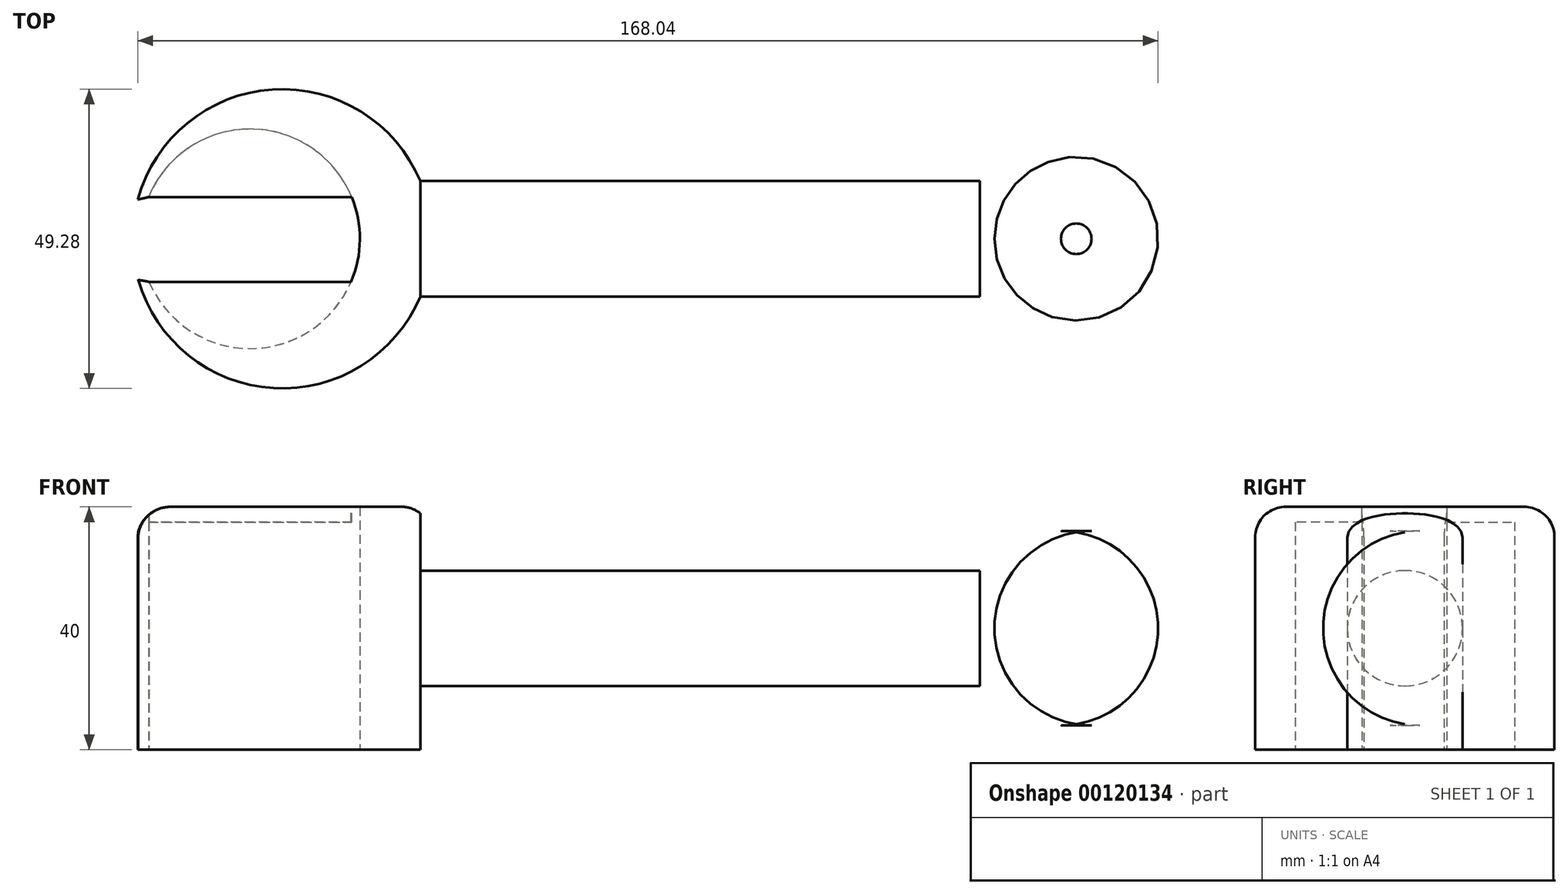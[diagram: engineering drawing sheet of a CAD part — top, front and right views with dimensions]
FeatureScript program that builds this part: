
annotation { "Feature Type Name" : "Feature", "Feature Type Description" : "" }
export const myFeature = defineFeature(function(context is Context, id is Id, definition is map)
    precondition{}
    {
        {
            var Q0;
            Q0=qCreatedBy(makeId("Top.planeOp"),FACE);
            var sketch = newSketch(context, id + "F0", { "sketchPlane" : qUnion([Q0])});
            skArc(sketch, "E0", {"start": v(-60.08, 17.67) * mm, "mid": v(-84.42, 32.76) * mm, "end": v(-106.6, 14.63) * mm});
            skLineSegment(sketch, "E1.bottom", {"start": v(-60.08, 17.67) * mm, "end": v(32.07, 17.67) * mm});
            skLineSegment(sketch, "E1.top", {"start": v(-60.08, -1.33) * mm, "end": v(32.07, -1.33) * mm});
            skPoint(sketch, "E2.start.orphan", {"position": v(39.84, 8.17) * mm});
            skPoint(sketch, "E3.end.orphan", {"position": v(-60.08, -1.33) * mm});
            skPoint(sketch, "E4.visualSharp", {"position": v(-82.82, 17.67) * mm});
            skPoint(sketch, "E5.visualSharp", {"position": v(-69.5, 8.17) * mm});
            skPoint(sketch, "E6.visualSharp", {"position": v(-82.82, -1.33) * mm});
            skLineSegment(sketch, "E7", {"start": v(-82.82, -5.13) * mm, "end": v(-82.82, -5.13) * mm});
            skArc(sketch, "E8.trimOffspring", {"start": v(-106.51, 1.41) * mm, "mid": v(-84.27, -16.43) * mm, "end": v(-60.08, -1.33) * mm});
            skPoint(sketch, "E9.orphan", {"position": v(-82.82, 22.17) * mm});
            skPoint(sketch, "E10.orphan", {"position": v(-69.5, 4.34) * mm});
            skPoint(sketch, "E11.visualSharp", {"position": v(-90.88, 19.61) * mm});
            skPoint(sketch, "E12.orphan", {"position": v(45.12, 19.04) * mm});
            skPoint(sketch, "E13.visualSharp", {"position": v(-91.65, -2.7) * mm});
            skLineSegment(sketch, "E14", {"start": v(-106.6, 14.63) * mm, "end": v(-104.83, 15.04) * mm});
            skLineSegment(sketch, "E15", {"start": v(-106.51, 1.41) * mm, "end": v(-104.74, 1.1) * mm});
            skLineSegment(sketch, "E16", {"start": v(-60.08, 17.67) * mm, "end": v(-60.08, -1.33) * mm});
            skPoint(sketch, "E17.orphan", {"position": v(39.84, 17.67) * mm});
            skPoint(sketch, "E18.center.orphan", {"position": v(45.12, 8.17) * mm});
            skPoint(sketch, "E19.orphan", {"position": v(39.84, -1.33) * mm});
            skPoint(sketch, "E20.center.orphan", {"position": v(47.96, 8.17) * mm});
            skArc(sketch, "E21", {"start": v(-104.74, 1.1) * mm, "mid": v(-70.03, 8.28) * mm, "end": v(-104.83, 15.04) * mm});
            skPoint(sketch, "E22.orphan", {"position": v(-90.88, 18.29) * mm});
            skPoint(sketch, "E23.orphan", {"position": v(-91.65, -1.28) * mm});
            skPoint(sketch, "E24.center.orphan", {"position": v(-89.28, 8.17) * mm});
            skPoint(sketch, "E25.right.end.orphan", {"position": v(57.82, -3.93) * mm});
            skArc(sketch, "E26", {"start": v(32.07, -1.33) * mm, "mid": v(66.48, 8.17) * mm, "end": v(32.07, 17.67) * mm});
            skPoint(sketch, "E27.end.orphan", {"position": v(36.17, -3.93) * mm});
            skPoint(sketch, "E28.left.end.orphan", {"position": v(36.17, 20.27) * mm});
            skPoint(sketch, "E28.bottom.start.orphan", {"position": v(36.17, 21.83) * mm});
            skCircle(sketch, "E29", {"center": v(-88.1, 8.17) * mm, "radius": 16.54 * mm});
            skPoint(sketch, "E30.center.orphan", {"position": v(46.23, 8.17) * mm});
            skPoint(sketch, "E31.trimOffspring.end.orphan", {"position": v(36.17, -1.33) * mm});
            skPoint(sketch, "E32.orphan", {"position": v(36.17, 17.67) * mm});
            skLineSegment(sketch, "E33", {"start": v(32.07, -1.33) * mm, "end": v(32.07, 17.67) * mm});
            skSolve(sketch);
        }
        {
            var Q0;
            Q0=makeQuery(id+"F0.imprint","IMPRINT",FACE,{"disambiguationData":[TD([[makeQuery(id+"F0.imprint","IMPRINT",EDGE,{"derivedFrom":sQuery(id+"F0.wireOp",EDGE,"E0")}),1.0]])]});
            extrude(context, id + "F1", {"entities" : qUnion([Q0]), "depth" : 20 * mm, "hasSecondDirection" : true, "secondDirectionOppositeDirection" : true, "secondDirectionDepth" : 20 * mm});
        }
        {
            var Q0;
            Q0=makeQuery(id+"F0.imprint","IMPRINT",FACE,{"disambiguationData":[TD([[makeQuery(id+"F0.imprint","IMPRINT",EDGE,{"derivedFrom":sQuery(id+"F0.wireOp",EDGE,"E1.bottom")}),-1.0]])]});
            extrude(context, id + "F2", {"entities" : qUnion([Q0]), "operationType" : NewBodyOperationType.ADD, "depth" : 9.5 * mm, "hasSecondDirection" : true, "secondDirectionOppositeDirection" : true, "secondDirectionDepth" : 9.5 * mm});
        }
        {
            var Q0;
            Q0=makeQuery(id+"F0.imprint","IMPRINT",FACE,{"disambiguationData":[TD([[makeQuery(id+"F0.imprint","IMPRINT",EDGE,{"derivedFrom":sQuery(id+"F0.wireOp",EDGE,"E26")}),1.0]])]});
            extrude(context, id + "F3", {"entities" : qUnion([Q0]), "depth" : 16 * mm, "hasSecondDirection" : true, "secondDirectionOppositeDirection" : true, "secondDirectionDepth" : 16 * mm});
        }
        {
            var Q0;
            Q0=makeQuery(id+"F3.opExtrude","CAP_EDGE",EDGE,{"disambiguationData":[OSD([sQuery(id+"F0.wireOp",EDGE,"E26")])],"isStart":true});
            var Q1;
            Q1=makeQuery(id+"F3.opExtrude","CAP_EDGE",EDGE,{"disambiguationData":[OSD([sQuery(id+"F0.wireOp",EDGE,"E26")])],"isStart":false});
            fillet(context, id + "F4", {"entities" : qUnion([Q0, Q1]), "radius" : 16 * mm, "tangentPropagation" : true, "allowEdgeOverflow" : false});
        }
        {
            var Q0;
            Q0=makeQuery(id+"F2.opExtrude","CAP_EDGE",EDGE,{"disambiguationData":[OSD([sQuery(id+"F0.wireOp",EDGE,"E1.top")])],"isStart":true});
            var Q1;
            Q1=makeQuery(id+"F2.opExtrude","CAP_EDGE",EDGE,{"disambiguationData":[OSD([sQuery(id+"F0.wireOp",EDGE,"E1.top")])],"isStart":false});
            var Q2;
            Q2=makeQuery(id+"F2.opExtrude","CAP_EDGE",EDGE,{"disambiguationData":[OSD([sQuery(id+"F0.wireOp",EDGE,"E1.bottom")])],"isStart":true});
            var Q3;
            Q3=makeQuery(id+"F2.opExtrude","CAP_EDGE",EDGE,{"disambiguationData":[OSD([sQuery(id+"F0.wireOp",EDGE,"E1.bottom")])],"isStart":false});
            fillet(context, id + "F5", {"entities" : qUnion([Q0, Q1, Q2, Q3]), "radius" : 9.5 * mm, "tangentPropagation" : true, "allowEdgeOverflow" : false});
        }
        {
            var Q0;
            Q0=makeQuery(id+"F1.opExtrude","CAP_FACE",FACE,{"disambiguationData":[OSD([sQuery(id+"F0.wireOp",EDGE,"E0"),sQuery(id+"F0.wireOp",EDGE,"E8.trimOffspring"),sQuery(id+"F0.wireOp",EDGE,"E14"),sQuery(id+"F0.wireOp",EDGE,"E15"),sQuery(id+"F0.wireOp",EDGE,"E16"),sQuery(id+"F0.wireOp",EDGE,"E21")])],"isStart":false});
            var sketch = newSketch(context, id + "F6", { "sketchPlane" : qUnion([Q0])});
            skLineSegment(sketch, "E34", {"start": v(-104.83, 15.04) * mm, "end": v(-71.38, 15.04) * mm});
            skLineSegment(sketch, "E35", {"start": v(-104.74, 1.1) * mm, "end": v(-71.47, 1.1) * mm});
            skSolve(sketch);
        }
        {
            var Q0;
            {var subQ0=sQuery(id+"F6.wireOp",EDGE,"E35");Q0=makeQuery(id+"F6.imprint","IMPRINT",FACE,{"disambiguationData":[TD([[makeQuery(id+"F6.imprint","IMPRINT",EDGE,{"derivedFrom":subQ0}),-1.0]])]});}
            var Q1;
            {var subQ0=sQuery(id+"F6.wireOp",EDGE,"E34");Q1=makeQuery(id+"F6.imprint","IMPRINT",FACE,{"disambiguationData":[TD([[makeQuery(id+"F6.imprint","IMPRINT",EDGE,{"derivedFrom":subQ0}),1.0]])]});}
            extrude(context, id + "F7", {"entities" : qUnion([Q0, Q1]), "operationType" : NewBodyOperationType.ADD, "oppositeDirection" : true, "depth" : 2.5 * mm});
        }
        {
            var Q0;
            Q0=makeQuery(id+"F1.opExtrude","CAP_EDGE",EDGE,{"disambiguationData":[OSD([sQuery(id+"F0.wireOp",EDGE,"E8.trimOffspring")])],"isStart":false});
            fillet(context, id + "F8", {"entities" : qUnion([Q0]), "radius" : 5 * mm, "tangentPropagation" : true, "allowEdgeOverflow" : false});
        }
    });
